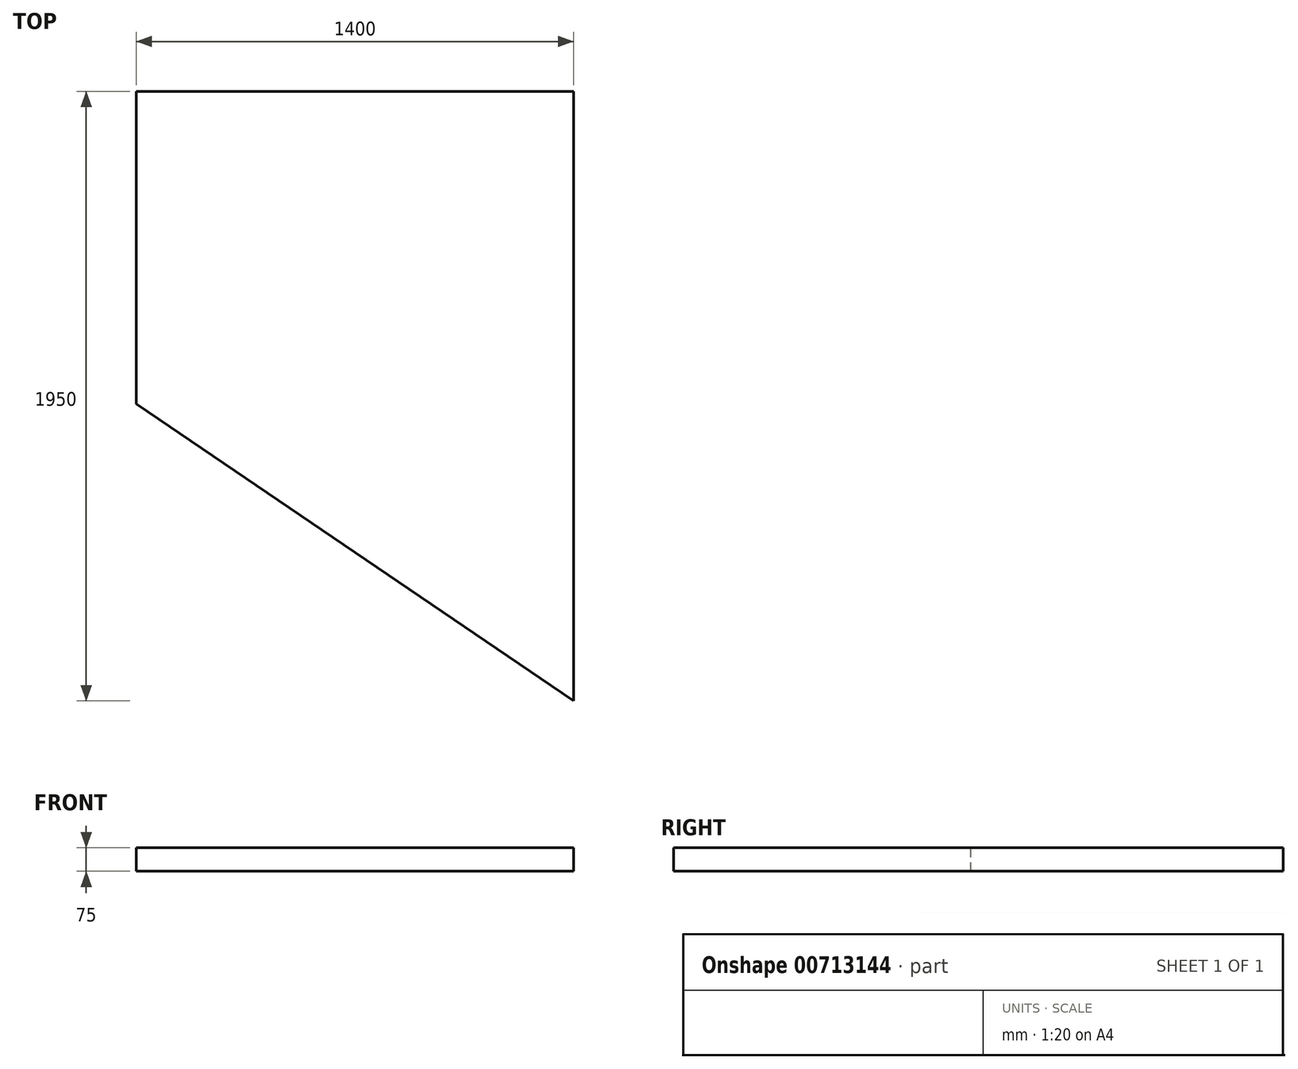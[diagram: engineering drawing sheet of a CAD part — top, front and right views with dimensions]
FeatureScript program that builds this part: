
annotation { "Feature Type Name" : "Feature", "Feature Type Description" : "" }
export const myFeature = defineFeature(function(context is Context, id is Id, definition is map)
    precondition{}
    {
        {
            var Q0;
            Q0=qCreatedBy(makeId("Top.planeOp"),FACE);
            var sketch = newSketch(context, id + "F0", { "sketchPlane" : qUnion([Q0])});
            skLineSegment(sketch, "E0", {"start": v(-1538.22, -138.35) * mm, "end": v(-1538.22, 861.65) * mm});
            skLineSegment(sketch, "E1", {"start": v(-1538.22, 861.65) * mm, "end": v(-138.22, 861.65) * mm});
            skLineSegment(sketch, "E2", {"start": v(-138.22, 861.65) * mm, "end": v(-138.22, -1088.35) * mm});
            skLineSegment(sketch, "E3", {"start": v(-138.22, -1088.35) * mm, "end": v(-1538.22, -138.35) * mm});
            skSolve(sketch);
        }
        {
            var Q0;
            Q0=makeQuery(id+"F0.imprint","IMPRINT",FACE,{"disambiguationData":[TD([[makeQuery(id+"F0.imprint","IMPRINT",EDGE,{"derivedFrom":sQuery(id+"F0.wireOp",EDGE,"E0")}),-1.0]])]});
            extrude(context, id + "F1", {"entities" : qUnion([Q0]), "depth" : 75 * mm, "offsetDistance" : 25 * mm});
        }
    });
